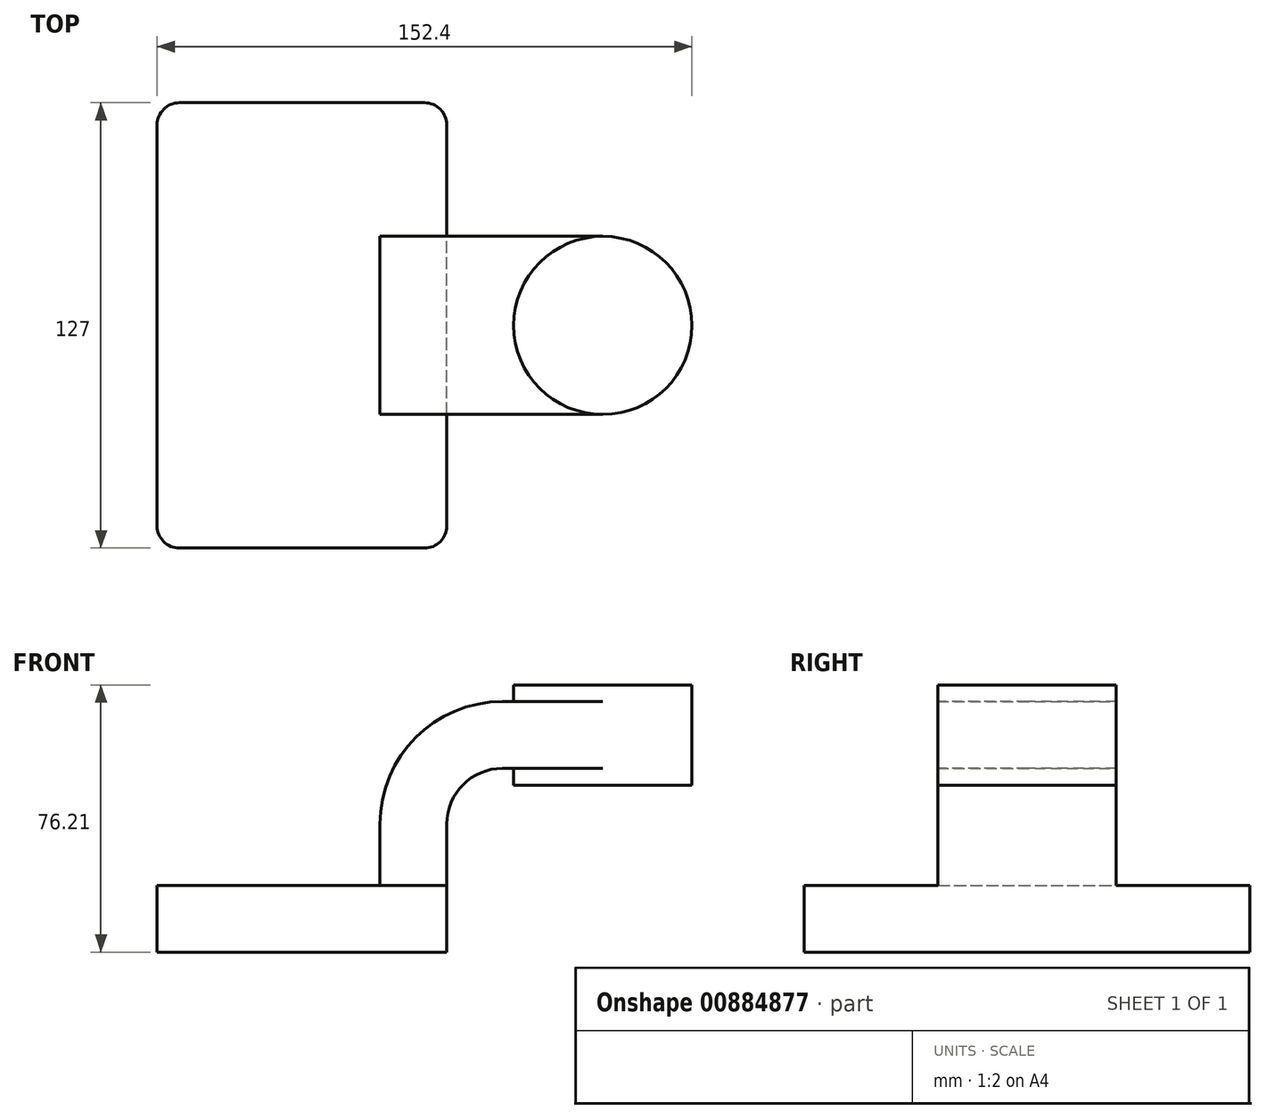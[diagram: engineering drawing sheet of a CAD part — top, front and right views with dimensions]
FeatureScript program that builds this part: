
annotation { "Feature Type Name" : "Feature", "Feature Type Description" : "" }
export const myFeature = defineFeature(function(context is Context, id is Id, definition is map)
    precondition{}
    {
        {
            var Q0;
            Q0=qCreatedBy(makeId("Front.planeOp"),FACE);
            var sketch = newSketch(context, id + "F0", { "sketchPlane" : qUnion([Q0])});
            skLineSegment(sketch, "E0.bottom", {"start": v(41.28, -9.52) * mm, "end": v(-41.27, -9.53) * mm});
            skLineSegment(sketch, "E0.top", {"start": v(41.27, 9.53) * mm, "end": v(-41.28, 9.53) * mm});
            skLineSegment(sketch, "E0.left", {"start": v(41.28, -9.52) * mm, "end": v(41.28, 9.53) * mm});
            skLineSegment(sketch, "E0.right", {"start": v(-41.27, -9.53) * mm, "end": v(-41.28, 9.53) * mm});
            skPoint(sketch, "E0.middle", {"position": v(0, 0) * mm});
            skLineSegment(sketch, "E1.bottom", {"start": v(60.32, 38.1) * mm, "end": v(111.13, 38.1) * mm});
            skLineSegment(sketch, "E1.top", {"start": v(60.32, 66.68) * mm, "end": v(111.12, 66.68) * mm});
            skLineSegment(sketch, "E1.left", {"start": v(60.32, 38.1) * mm, "end": v(60.32, 66.68) * mm});
            skLineSegment(sketch, "E1.right", {"start": v(111.13, 38.1) * mm, "end": v(111.12, 66.68) * mm});
            skPoint(sketch, "E1.middle", {"position": v(85.72, 52.39) * mm});
            skLineSegment(sketch, "E2", {"start": v(41.27, 9.53) * mm, "end": v(41.27, 27) * mm});
            skArc(sketch, "E3", {"start": v(41.27, 27) * mm, "mid": v(45.92, 38.23) * mm, "end": v(57.15, 42.88) * mm});
            skLineSegment(sketch, "E4", {"start": v(57.15, 42.88) * mm, "end": v(85.73, 42.88) * mm});
            skPoint(sketch, "E4.endSnap0", {"position": v(85.73, 38.1) * mm});
            skLineSegment(sketch, "E5.0", {"start": v(57.15, 61.93) * mm, "end": v(85.73, 61.93) * mm});
            skArc(sketch, "E5.1", {"start": v(22.23, 27) * mm, "mid": v(32.45, 51.7) * mm, "end": v(57.15, 61.93) * mm});
            skLineSegment(sketch, "E5.2", {"start": v(22.22, 9.53) * mm, "end": v(22.22, 27) * mm});
            skLineSegment(sketch, "E6", {"start": v(85.72, 38.1) * mm, "end": v(85.72, 66.68) * mm});
            skFitSpline(sketch, "E7", {"points": [v(-41.28, 9.52) * mm, v(57.15, 61.93) * mm], "startDerivative": vector(19.77, 89.28) * mm, "endDerivative": vector(122.6, -5.2) * mm});
            skSolve(sketch);
        }
        {
            var Q0;
            Q0=makeQuery(id+"F0.imprint","IMPRINT",FACE,{"disambiguationData":[TD([[makeQuery(id+"F0.imprint","IMPRINT",EDGE,{"derivedFrom":sQuery(id+"F0.wireOp",EDGE,"E0.bottom")}),-1.0]])]});
            extrude(context, id + "F1", {"entities" : qUnion([Q0]), "endBound" : BoundingType.SYMMETRIC, "depth" : 127 * mm, "offsetDistance" : 25.4 * mm});
        }
        {
            var Q0;
            {var subQ1=sQuery(id+"F0.wireOp",EDGE,"E2");Q0=makeQuery(id+"F0.imprint","IMPRINT",FACE,{"disambiguationData":[TD([[makeQuery(id+"F0.imprint","IMPRINT",EDGE,{"derivedFrom":subQ1}),1.0]])]});}
            var Q1;
            {var subQ0=sQuery(id+"F0.wireOp",EDGE,"E4");var subQ1=sQuery(id+"F0.wireOp",EDGE,"E1.left");var subQ2=makeQuery(id+"F0.imprint","INTERSECT",VERTEX,{"derivedFrom":[subQ1,subQ0]});Q1=makeQuery(id+"F0.imprint","IMPRINT",FACE,{"disambiguationData":[TD([[makeQuery(id+"F0.imprint","IMPRINT",EDGE,{"disambiguationData":[TD([[subQ2,-1.0]])],"derivedFrom":subQ1}),-1.0]])]});}
            extrude(context, id + "F2", {"entities" : qUnion([Q0, Q1]), "operationType" : NewBodyOperationType.ADD, "endBound" : BoundingType.SYMMETRIC, "depth" : 50.8 * mm, "offsetDistance" : 25.4 * mm});
        }
        {
            var Q0;
            Q0=makeQuery(id+"F0.imprint","IMPRINT",FACE,{"disambiguationData":[TD([[makeQuery(id+"F0.imprint","IMPRINT",EDGE,{"derivedFrom":sQuery(id+"F0.wireOp",EDGE,"E5.1")}),1.0]])]});
            extrude(context, id + "F3", {"entities" : qUnion([Q0]), "operationType" : NewBodyOperationType.ADD, "endBound" : BoundingType.SYMMETRIC, "depth" : 15.88 * mm, "offsetDistance" : 25.4 * mm});
        }
        {
            var Q0;
            {var subQ0=sQuery(id+"F0.wireOp",EDGE,"E1.right");Q0=makeQuery(id+"F0.imprint","IMPRINT",FACE,{"disambiguationData":[TD([[makeQuery(id+"F0.imprint","IMPRINT",EDGE,{"derivedFrom":subQ0}),1.0]])]});}
            var Q1;
            Q1=sQuery(id+"F0.wireOp",EDGE,"E6");
            revolve(context, id + "F4", {"operationType" : NewBodyOperationType.ADD, "surfaceOperationType" : NewSurfaceOperationType.NEW, "entities" : qUnion([Q0]), "axis" : qUnion([Q1]), "revolveType" : RevolveType.FULL});
        }
        {
            var Q0;
            Q0=makeQuery(id+"F1.opExtrude","CAP_EDGE",EDGE,{"disambiguationData":[OSD([sQuery(id+"F0.wireOp",EDGE,"E0.left")])],"isStart":false});
            var Q1;
            Q1=makeQuery(id+"F1.opExtrude","CAP_EDGE",EDGE,{"disambiguationData":[OSD([sQuery(id+"F0.wireOp",EDGE,"E0.right")])],"isStart":false});
            var Q2;
            Q2=makeQuery(id+"F1.opExtrude","CAP_EDGE",EDGE,{"disambiguationData":[OSD([sQuery(id+"F0.wireOp",EDGE,"E0.left")])],"isStart":true});
            var Q3;
            Q3=makeQuery(id+"F1.opExtrude","CAP_EDGE",EDGE,{"disambiguationData":[OSD([sQuery(id+"F0.wireOp",EDGE,"E0.right")])],"isStart":true});
            fillet(context, id + "F5", {"entities" : qUnion([Q0, Q1, Q2, Q3]), "radius" : 6.35 * mm, "tangentPropagation" : true, "allowEdgeOverflow" : false});
        }
    });
